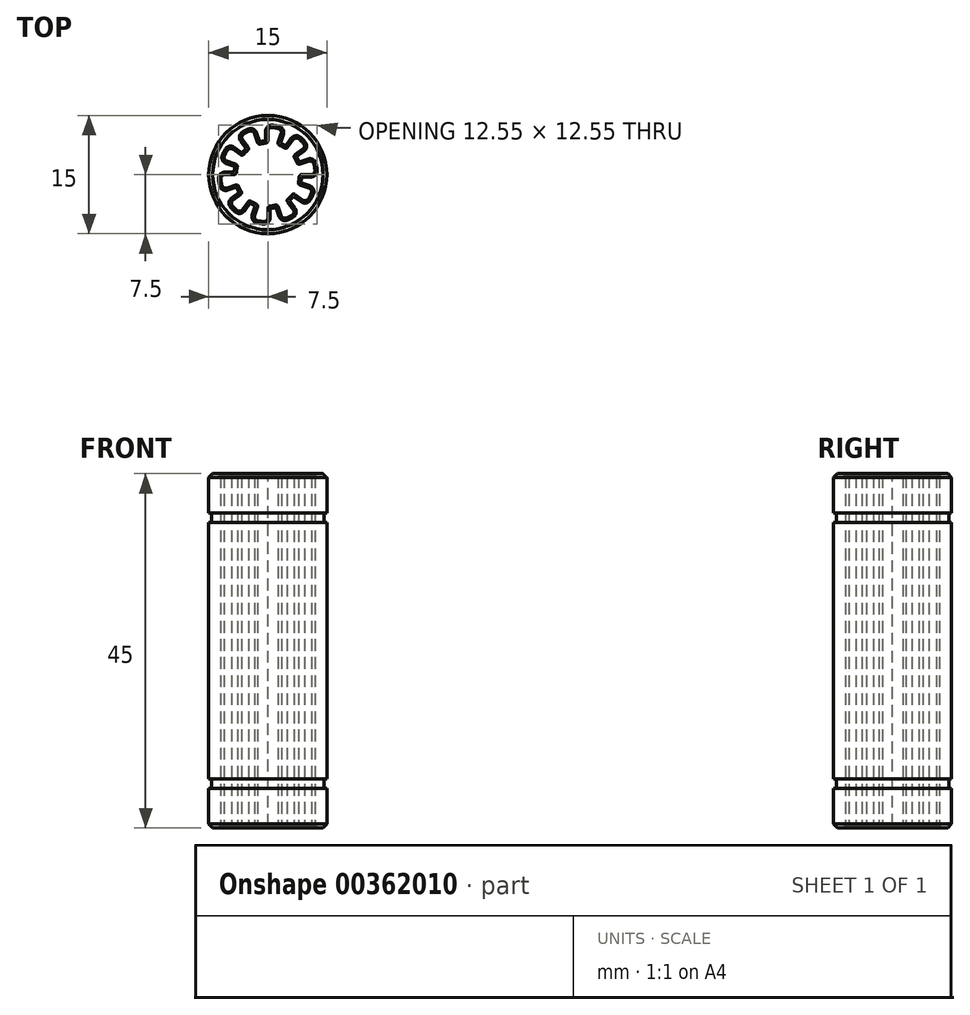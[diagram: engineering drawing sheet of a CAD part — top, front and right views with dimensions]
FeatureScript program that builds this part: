
annotation { "Feature Type Name" : "Feature", "Feature Type Description" : "" }
export const myFeature = defineFeature(function(context is Context, id is Id, definition is map)
    precondition{}
    {
        {
            var Q0;
            Q0=qCreatedBy(makeId("Top.planeOp"),FACE);
            var sketch = newSketch(context, id + "F0", { "sketchPlane" : qUnion([Q0])});
            skCircle(sketch, "E0", {"center": v(0, 0) * mm, "radius": 7.5 * mm});
            skLineSegment(sketch, "E1", {"start": v(0, 0) * mm, "end": v(0, 8.95) * mm, "construction": true});
            skLineSegment(sketch, "E2", {"start": v(0, 0) * mm, "end": v(5.23, 7.2) * mm, "construction": true});
            skArc(sketch, "E3", {"start": v(2.35, 3.24) * mm, "mid": v(1.82, 3.56) * mm, "end": v(1.24, 3.8) * mm});
            skArc(sketch, "E4", {"start": v(0, 6) * mm, "mid": v(0.94, 5.93) * mm, "end": v(1.85, 5.7) * mm});
            skLineSegment(sketch, "E5", {"start": v(1.85, 5.7) * mm, "end": v(1.24, 3.8) * mm});
            skLineSegment(sketch, "E6", {"start": v(2.35, 3.24) * mm, "end": v(3.53, 4.85) * mm});
            skArc(sketch, "E7", {"start": v(1.85, 5.7) * mm, "mid": v(2.72, 5.35) * mm, "end": v(3.53, 4.85) * mm, "construction": true});
            skLineSegment(sketch, "E8.1.0", {"start": v(0, 4) * mm, "end": v(0, 6) * mm});
            skArc(sketch, "E8.1.1", {"start": v(0, 4) * mm, "mid": v(-0.63, 3.95) * mm, "end": v(-1.24, 3.8) * mm});
            skLineSegment(sketch, "E8.1.2", {"start": v(-1.85, 5.7) * mm, "end": v(-1.24, 3.8) * mm});
            skArc(sketch, "E8.1.3", {"start": v(-3.53, 4.85) * mm, "mid": v(-2.72, 5.35) * mm, "end": v(-1.85, 5.7) * mm});
            skLineSegment(sketch, "E8.2.0", {"start": v(-2.35, 3.24) * mm, "end": v(-3.53, 4.85) * mm});
            skArc(sketch, "E8.2.1", {"start": v(-2.35, 3.24) * mm, "mid": v(-2.83, 2.83) * mm, "end": v(-3.24, 2.35) * mm});
            skLineSegment(sketch, "E8.2.2", {"start": v(-4.85, 3.53) * mm, "end": v(-3.24, 2.35) * mm});
            skArc(sketch, "E8.2.3", {"start": v(-5.7, 1.85) * mm, "mid": v(-5.35, 2.72) * mm, "end": v(-4.85, 3.53) * mm});
            skLineSegment(sketch, "E8.3.0", {"start": v(-3.8, 1.24) * mm, "end": v(-5.7, 1.85) * mm});
            skArc(sketch, "E8.3.1", {"start": v(-3.8, 1.24) * mm, "mid": v(-3.95, 0.63) * mm, "end": v(-4, 0) * mm});
            skLineSegment(sketch, "E8.3.2", {"start": v(-6, 0) * mm, "end": v(-4, 0) * mm});
            skArc(sketch, "E8.3.3", {"start": v(-5.7, -1.85) * mm, "mid": v(-5.93, -0.94) * mm, "end": v(-6, 0) * mm});
            skLineSegment(sketch, "E8.4.0", {"start": v(-3.8, -1.24) * mm, "end": v(-5.7, -1.85) * mm});
            skArc(sketch, "E8.4.1", {"start": v(-3.8, -1.24) * mm, "mid": v(-3.56, -1.82) * mm, "end": v(-3.24, -2.35) * mm});
            skLineSegment(sketch, "E8.4.2", {"start": v(-4.85, -3.53) * mm, "end": v(-3.24, -2.35) * mm});
            skArc(sketch, "E8.4.3", {"start": v(-3.53, -4.85) * mm, "mid": v(-4.24, -4.24) * mm, "end": v(-4.85, -3.53) * mm});
            skLineSegment(sketch, "E8.5.0", {"start": v(-2.35, -3.24) * mm, "end": v(-3.53, -4.85) * mm});
            skArc(sketch, "E8.5.1", {"start": v(-2.35, -3.24) * mm, "mid": v(-1.82, -3.56) * mm, "end": v(-1.24, -3.8) * mm});
            skLineSegment(sketch, "E8.5.2", {"start": v(-1.85, -5.7) * mm, "end": v(-1.24, -3.8) * mm});
            skArc(sketch, "E8.5.3", {"start": v(0, -6) * mm, "mid": v(-0.94, -5.93) * mm, "end": v(-1.85, -5.7) * mm});
            skLineSegment(sketch, "E8.6.0", {"start": v(0, -4) * mm, "end": v(0, -6) * mm});
            skArc(sketch, "E8.6.1", {"start": v(0, -4) * mm, "mid": v(0.63, -3.95) * mm, "end": v(1.24, -3.8) * mm});
            skLineSegment(sketch, "E8.6.2", {"start": v(1.85, -5.7) * mm, "end": v(1.24, -3.8) * mm});
            skArc(sketch, "E8.6.3", {"start": v(3.53, -4.85) * mm, "mid": v(2.72, -5.35) * mm, "end": v(1.85, -5.7) * mm});
            skLineSegment(sketch, "E8.7.0", {"start": v(2.35, -3.24) * mm, "end": v(3.53, -4.85) * mm});
            skArc(sketch, "E8.7.1", {"start": v(2.35, -3.24) * mm, "mid": v(2.83, -2.83) * mm, "end": v(3.24, -2.35) * mm});
            skLineSegment(sketch, "E8.7.2", {"start": v(4.85, -3.53) * mm, "end": v(3.24, -2.35) * mm});
            skArc(sketch, "E8.7.3", {"start": v(5.7, -1.85) * mm, "mid": v(5.35, -2.72) * mm, "end": v(4.85, -3.53) * mm});
            skLineSegment(sketch, "E8.8.0", {"start": v(3.8, -1.24) * mm, "end": v(5.7, -1.85) * mm});
            skArc(sketch, "E8.8.1", {"start": v(3.8, -1.24) * mm, "mid": v(3.95, -0.63) * mm, "end": v(4, 0) * mm});
            skLineSegment(sketch, "E8.8.2", {"start": v(6, 0) * mm, "end": v(4, 0) * mm});
            skArc(sketch, "E8.8.3", {"start": v(5.7, 1.85) * mm, "mid": v(5.93, 0.94) * mm, "end": v(6, 0) * mm});
            skLineSegment(sketch, "E8.9.0", {"start": v(3.8, 1.24) * mm, "end": v(5.7, 1.85) * mm});
            skArc(sketch, "E8.9.1", {"start": v(3.8, 1.24) * mm, "mid": v(3.56, 1.82) * mm, "end": v(3.24, 2.35) * mm});
            skLineSegment(sketch, "E8.9.2", {"start": v(4.85, 3.53) * mm, "end": v(3.24, 2.35) * mm});
            skArc(sketch, "E8.9.3", {"start": v(3.53, 4.85) * mm, "mid": v(4.24, 4.24) * mm, "end": v(4.85, 3.53) * mm});
            skSolve(sketch);
        }
        {
            var Q0;
            Q0=makeQuery(id+"F0.imprint","IMPRINT",FACE,{"disambiguationData":[TD([[makeQuery(id+"F0.imprint","IMPRINT",EDGE,{"derivedFrom":sQuery(id+"F0.wireOp",EDGE,"E0")}),1.0]])]});
            extrude(context, id + "F1", {"entities" : qUnion([Q0]), "depth" : 45 * mm});
        }
        {
            var Q0;
            Q0=qCreatedBy(makeId("Top.planeOp"),FACE);
            cPlane(context, id + "F2", {"entities" : qUnion([Q0]), "cplaneType" : CPlaneType.OFFSET, "offset" : 5 * mm, "width" : 150 * mm, "height" : 150 * mm});
        }
        {
            var Q0;
            Q0=qCreatedBy(id+"F2.planeOp",FACE);
            var sketch = newSketch(context, id + "F3", { "sketchPlane" : qUnion([Q0])});
            skCircle(sketch, "E9", {"center": v(0, 0) * mm, "radius": 7.15 * mm});
            skCircle(sketch, "E10", {"center": v(0, 0) * mm, "radius": 8 * mm});
            skSolve(sketch);
        }
        {
            var Q0;
            Q0 = qSketchRegion(id + "F3", true);
            extrude(context, id + "F4", {"entities" : qUnion([Q0]), "operationType" : NewBodyOperationType.REMOVE, "depth" : 1.2 * mm});
        }
        {
            var Q0;
            Q0=qCreatedBy(makeId("Top.planeOp"),FACE);
            cPlane(context, id + "F5", {"entities" : qUnion([Q0]), "cplaneType" : CPlaneType.OFFSET, "offset" : (45 - 5) * mm, "width" : 150 * mm, "height" : 150 * mm});
        }
        {
            var Q0;
            Q0=qCreatedBy(id+"F5.planeOp",FACE);
            var sketch = newSketch(context, id + "F6", { "sketchPlane" : qUnion([Q0])});
            skCircle(sketch, "E11", {"center": v(0, 0) * mm, "radius": 8 * mm});
            skCircle(sketch, "E12", {"center": v(0, 0) * mm, "radius": 7.15 * mm});
            skSolve(sketch);
        }
        {
            var Q0;
            Q0 = qSketchRegion(id + "F6", true);
            extrude(context, id + "F7", {"entities" : qUnion([Q0]), "operationType" : NewBodyOperationType.REMOVE, "oppositeDirection" : true, "depth" : 1.2 * mm});
        }
        {
            var Q0;
            Q0=makeQuery(id+"F1.opExtrude","CAP_EDGE",EDGE,{"disambiguationData":[OSD([sQuery(id+"F0.wireOp",EDGE,"E0")])],"isStart":false});
            var Q1;
            Q1=makeQuery(id+"F1.opExtrude","CAP_EDGE",EDGE,{"disambiguationData":[OSD([sQuery(id+"F0.wireOp",EDGE,"E0")])],"isStart":true});
            chamfer(context, id + "F8", {"entities" : qUnion([Q0, Q1]), "width" : 0.5 * mm, "tangentPropagation" : true});
        }
        {
            var Q0;
            Q0=makeQuery(id+"F1.opExtrude","SWEPT_EDGE",EDGE,{"disambiguationData":[OSD([sQuery(id+"F0.wireOp",EDGE,"E3"),sQuery(id+"F0.wireOp",EDGE,"E6")])]});
            var Q1;
            Q1=makeQuery(id+"F1.opExtrude","SWEPT_EDGE",EDGE,{"disambiguationData":[OSD([sQuery(id+"F0.wireOp",EDGE,"E3"),sQuery(id+"F0.wireOp",EDGE,"E5")])]});
            var Q2;
            Q2=makeQuery(id+"F1.opExtrude","SWEPT_EDGE",EDGE,{"disambiguationData":[OSD([sQuery(id+"F0.wireOp",EDGE,"045b818b-034f-4962-901c-0fb9900f9058.3.11.0"),sQuery(id+"F0.wireOp",EDGE,"045b818b-034f-4962-901c-0fb9900f9058.7.11.0")])]});
            var Q3;
            Q3=makeQuery(id+"F1.opExtrude","SWEPT_EDGE",EDGE,{"disambiguationData":[OSD([sQuery(id+"F0.wireOp",EDGE,"045b818b-034f-4962-901c-0fb9900f9058.3.11.0"),sQuery(id+"F0.wireOp",EDGE,"045b818b-034f-4962-901c-0fb9900f9058.6.11.0")])]});
            var Q4;
            Q4=makeQuery(id+"F1.opExtrude","SWEPT_EDGE",EDGE,{"disambiguationData":[OSD([sQuery(id+"F0.wireOp",EDGE,"045b818b-034f-4962-901c-0fb9900f9058.3.10.0"),sQuery(id+"F0.wireOp",EDGE,"045b818b-034f-4962-901c-0fb9900f9058.7.10.0")])]});
            var Q5;
            Q5=makeQuery(id+"F1.opExtrude","SWEPT_EDGE",EDGE,{"disambiguationData":[OSD([sQuery(id+"F0.wireOp",EDGE,"045b818b-034f-4962-901c-0fb9900f9058.3.10.0"),sQuery(id+"F0.wireOp",EDGE,"045b818b-034f-4962-901c-0fb9900f9058.6.10.0")])]});
            var Q6;
            Q6=makeQuery(id+"F1.opExtrude","SWEPT_EDGE",EDGE,{"disambiguationData":[OSD([sQuery(id+"F0.wireOp",EDGE,"E8.9.1"),sQuery(id+"F0.wireOp",EDGE,"E8.9.2")])]});
            var Q7;
            Q7=makeQuery(id+"F1.opExtrude","SWEPT_EDGE",EDGE,{"disambiguationData":[OSD([sQuery(id+"F0.wireOp",EDGE,"E8.9.0"),sQuery(id+"F0.wireOp",EDGE,"E8.9.1")])]});
            var Q8;
            Q8=makeQuery(id+"F1.opExtrude","SWEPT_EDGE",EDGE,{"disambiguationData":[OSD([sQuery(id+"F0.wireOp",EDGE,"E8.8.1"),sQuery(id+"F0.wireOp",EDGE,"E8.8.2")])]});
            var Q9;
            Q9=makeQuery(id+"F1.opExtrude","SWEPT_EDGE",EDGE,{"disambiguationData":[OSD([sQuery(id+"F0.wireOp",EDGE,"E8.8.0"),sQuery(id+"F0.wireOp",EDGE,"E8.8.1")])]});
            var Q10;
            Q10=makeQuery(id+"F1.opExtrude","SWEPT_EDGE",EDGE,{"disambiguationData":[OSD([sQuery(id+"F0.wireOp",EDGE,"E8.7.1"),sQuery(id+"F0.wireOp",EDGE,"E8.7.2")])]});
            var Q11;
            Q11=makeQuery(id+"F1.opExtrude","SWEPT_EDGE",EDGE,{"disambiguationData":[OSD([sQuery(id+"F0.wireOp",EDGE,"E8.7.0"),sQuery(id+"F0.wireOp",EDGE,"E8.7.1")])]});
            var Q12;
            Q12=makeQuery(id+"F1.opExtrude","SWEPT_EDGE",EDGE,{"disambiguationData":[OSD([sQuery(id+"F0.wireOp",EDGE,"E8.6.1"),sQuery(id+"F0.wireOp",EDGE,"E8.6.2")])]});
            var Q13;
            Q13=makeQuery(id+"F1.opExtrude","SWEPT_EDGE",EDGE,{"disambiguationData":[OSD([sQuery(id+"F0.wireOp",EDGE,"E8.6.0"),sQuery(id+"F0.wireOp",EDGE,"E8.6.1")])]});
            var Q14;
            Q14=makeQuery(id+"F1.opExtrude","SWEPT_EDGE",EDGE,{"disambiguationData":[OSD([sQuery(id+"F0.wireOp",EDGE,"E8.5.1"),sQuery(id+"F0.wireOp",EDGE,"E8.5.2")])]});
            var Q15;
            Q15=makeQuery(id+"F1.opExtrude","SWEPT_EDGE",EDGE,{"disambiguationData":[OSD([sQuery(id+"F0.wireOp",EDGE,"E8.5.0"),sQuery(id+"F0.wireOp",EDGE,"E8.5.1")])]});
            var Q16;
            Q16=makeQuery(id+"F1.opExtrude","SWEPT_EDGE",EDGE,{"disambiguationData":[OSD([sQuery(id+"F0.wireOp",EDGE,"E8.4.1"),sQuery(id+"F0.wireOp",EDGE,"E8.4.2")])]});
            var Q17;
            Q17=makeQuery(id+"F1.opExtrude","SWEPT_EDGE",EDGE,{"disambiguationData":[OSD([sQuery(id+"F0.wireOp",EDGE,"E8.4.0"),sQuery(id+"F0.wireOp",EDGE,"E8.4.1")])]});
            var Q18;
            Q18=makeQuery(id+"F1.opExtrude","SWEPT_EDGE",EDGE,{"disambiguationData":[OSD([sQuery(id+"F0.wireOp",EDGE,"E8.3.1"),sQuery(id+"F0.wireOp",EDGE,"E8.3.2")])]});
            var Q19;
            Q19=makeQuery(id+"F1.opExtrude","SWEPT_EDGE",EDGE,{"disambiguationData":[OSD([sQuery(id+"F0.wireOp",EDGE,"E8.3.0"),sQuery(id+"F0.wireOp",EDGE,"E8.3.1")])]});
            var Q20;
            Q20=makeQuery(id+"F1.opExtrude","SWEPT_EDGE",EDGE,{"disambiguationData":[OSD([sQuery(id+"F0.wireOp",EDGE,"E8.2.1"),sQuery(id+"F0.wireOp",EDGE,"E8.2.2")])]});
            var Q21;
            Q21=makeQuery(id+"F1.opExtrude","SWEPT_EDGE",EDGE,{"disambiguationData":[OSD([sQuery(id+"F0.wireOp",EDGE,"E8.2.0"),sQuery(id+"F0.wireOp",EDGE,"E8.2.1")])]});
            var Q22;
            Q22=makeQuery(id+"F1.opExtrude","SWEPT_EDGE",EDGE,{"disambiguationData":[OSD([sQuery(id+"F0.wireOp",EDGE,"E8.1.1"),sQuery(id+"F0.wireOp",EDGE,"E8.1.2")])]});
            var Q23;
            Q23=makeQuery(id+"F1.opExtrude","SWEPT_EDGE",EDGE,{"disambiguationData":[OSD([sQuery(id+"F0.wireOp",EDGE,"E8.1.0"),sQuery(id+"F0.wireOp",EDGE,"E8.1.1")])]});
            fillet(context, id + "F9", {"entities" : qUnion([Q0, Q1, Q2, Q3, Q4, Q5, Q6, Q7, Q8, Q9, Q10, Q11, Q12, Q13, Q14, Q15, Q16, Q17, Q18, Q19, Q20, Q21, Q22, Q23]), "radius" : 0.3 * mm, "tangentPropagation" : true, "allowEdgeOverflow" : false});
        }
        {
            var Q0;
            Q0=makeQuery(id+"F1.opExtrude","SWEPT_EDGE",EDGE,{"disambiguationData":[OSD([sQuery(id+"F0.wireOp",EDGE,"045b818b-034f-4962-901c-0fb9900f9058.7.11.0"),sQuery(id+"F0.wireOp",EDGE,"045b818b-034f-4962-901c-0fb9900f9058.10.11.0")])]});
            var Q1;
            Q1=makeQuery(id+"F1.opExtrude","SWEPT_EDGE",EDGE,{"disambiguationData":[OSD([sQuery(id+"F0.wireOp",EDGE,"E6"),sQuery(id+"F0.wireOp",EDGE,"045b818b-034f-4962-901c-0fb9900f9058.10.11.0")])]});
            var Q2;
            Q2=makeQuery(id+"F1.opExtrude","SWEPT_EDGE",EDGE,{"disambiguationData":[OSD([sQuery(id+"F0.wireOp",EDGE,"E4"),sQuery(id+"F0.wireOp",EDGE,"E8.1.0")])]});
            var Q3;
            Q3=makeQuery(id+"F1.opExtrude","SWEPT_EDGE",EDGE,{"disambiguationData":[OSD([sQuery(id+"F0.wireOp",EDGE,"E4"),sQuery(id+"F0.wireOp",EDGE,"E5")])]});
            var Q4;
            Q4=makeQuery(id+"F1.opExtrude","SWEPT_EDGE",EDGE,{"disambiguationData":[OSD([sQuery(id+"F0.wireOp",EDGE,"045b818b-034f-4962-901c-0fb9900f9058.10.10.0"),sQuery(id+"F0.wireOp",EDGE,"045b818b-034f-4962-901c-0fb9900f9058.6.11.0")])]});
            var Q5;
            Q5=makeQuery(id+"F1.opExtrude","SWEPT_EDGE",EDGE,{"disambiguationData":[OSD([sQuery(id+"F0.wireOp",EDGE,"045b818b-034f-4962-901c-0fb9900f9058.7.10.0"),sQuery(id+"F0.wireOp",EDGE,"045b818b-034f-4962-901c-0fb9900f9058.10.10.0")])]});
            var Q6;
            Q6=makeQuery(id+"F1.opExtrude","SWEPT_EDGE",EDGE,{"disambiguationData":[OSD([sQuery(id+"F0.wireOp",EDGE,"E8.9.3"),sQuery(id+"F0.wireOp",EDGE,"045b818b-034f-4962-901c-0fb9900f9058.6.10.0")])]});
            var Q7;
            Q7=makeQuery(id+"F1.opExtrude","SWEPT_EDGE",EDGE,{"disambiguationData":[OSD([sQuery(id+"F0.wireOp",EDGE,"E8.9.2"),sQuery(id+"F0.wireOp",EDGE,"E8.9.3")])]});
            var Q8;
            Q8=makeQuery(id+"F1.opExtrude","SWEPT_EDGE",EDGE,{"disambiguationData":[OSD([sQuery(id+"F0.wireOp",EDGE,"E8.8.3"),sQuery(id+"F0.wireOp",EDGE,"E8.9.0")])]});
            var Q9;
            Q9=makeQuery(id+"F1.opExtrude","SWEPT_EDGE",EDGE,{"disambiguationData":[OSD([sQuery(id+"F0.wireOp",EDGE,"E8.8.2"),sQuery(id+"F0.wireOp",EDGE,"E8.8.3")])]});
            var Q10;
            Q10=makeQuery(id+"F1.opExtrude","SWEPT_EDGE",EDGE,{"disambiguationData":[OSD([sQuery(id+"F0.wireOp",EDGE,"E8.7.3"),sQuery(id+"F0.wireOp",EDGE,"E8.8.0")])]});
            var Q11;
            Q11=makeQuery(id+"F1.opExtrude","SWEPT_EDGE",EDGE,{"disambiguationData":[OSD([sQuery(id+"F0.wireOp",EDGE,"E8.7.2"),sQuery(id+"F0.wireOp",EDGE,"E8.7.3")])]});
            var Q12;
            Q12=makeQuery(id+"F1.opExtrude","SWEPT_EDGE",EDGE,{"disambiguationData":[OSD([sQuery(id+"F0.wireOp",EDGE,"E8.6.3"),sQuery(id+"F0.wireOp",EDGE,"E8.7.0")])]});
            var Q13;
            Q13=makeQuery(id+"F1.opExtrude","SWEPT_EDGE",EDGE,{"disambiguationData":[OSD([sQuery(id+"F0.wireOp",EDGE,"E8.6.2"),sQuery(id+"F0.wireOp",EDGE,"E8.6.3")])]});
            var Q14;
            Q14=makeQuery(id+"F1.opExtrude","SWEPT_EDGE",EDGE,{"disambiguationData":[OSD([sQuery(id+"F0.wireOp",EDGE,"E8.5.2"),sQuery(id+"F0.wireOp",EDGE,"E8.5.3")])]});
            var Q15;
            Q15=makeQuery(id+"F1.opExtrude","SWEPT_EDGE",EDGE,{"disambiguationData":[OSD([sQuery(id+"F0.wireOp",EDGE,"E8.5.3"),sQuery(id+"F0.wireOp",EDGE,"E8.6.0")])]});
            var Q16;
            Q16=makeQuery(id+"F1.opExtrude","SWEPT_EDGE",EDGE,{"disambiguationData":[OSD([sQuery(id+"F0.wireOp",EDGE,"E8.4.3"),sQuery(id+"F0.wireOp",EDGE,"E8.5.0")])]});
            var Q17;
            Q17=makeQuery(id+"F1.opExtrude","SWEPT_EDGE",EDGE,{"disambiguationData":[OSD([sQuery(id+"F0.wireOp",EDGE,"E8.4.2"),sQuery(id+"F0.wireOp",EDGE,"E8.4.3")])]});
            var Q18;
            Q18=makeQuery(id+"F1.opExtrude","SWEPT_EDGE",EDGE,{"disambiguationData":[OSD([sQuery(id+"F0.wireOp",EDGE,"E8.3.3"),sQuery(id+"F0.wireOp",EDGE,"E8.4.0")])]});
            var Q19;
            Q19=makeQuery(id+"F1.opExtrude","SWEPT_EDGE",EDGE,{"disambiguationData":[OSD([sQuery(id+"F0.wireOp",EDGE,"E8.3.2"),sQuery(id+"F0.wireOp",EDGE,"E8.3.3")])]});
            var Q20;
            Q20=makeQuery(id+"F1.opExtrude","SWEPT_EDGE",EDGE,{"disambiguationData":[OSD([sQuery(id+"F0.wireOp",EDGE,"E8.2.3"),sQuery(id+"F0.wireOp",EDGE,"E8.3.0")])]});
            var Q21;
            Q21=makeQuery(id+"F1.opExtrude","SWEPT_EDGE",EDGE,{"disambiguationData":[OSD([sQuery(id+"F0.wireOp",EDGE,"E8.2.2"),sQuery(id+"F0.wireOp",EDGE,"E8.2.3")])]});
            var Q22;
            Q22=makeQuery(id+"F1.opExtrude","SWEPT_EDGE",EDGE,{"disambiguationData":[OSD([sQuery(id+"F0.wireOp",EDGE,"E8.1.3"),sQuery(id+"F0.wireOp",EDGE,"E8.2.0")])]});
            var Q23;
            Q23=makeQuery(id+"F1.opExtrude","SWEPT_EDGE",EDGE,{"disambiguationData":[OSD([sQuery(id+"F0.wireOp",EDGE,"E8.1.2"),sQuery(id+"F0.wireOp",EDGE,"E8.1.3")])]});
            fillet(context, id + "F10", {"entities" : qUnion([Q0, Q1, Q2, Q3, Q4, Q5, Q6, Q7, Q8, Q9, Q10, Q11, Q12, Q13, Q14, Q15, Q16, Q17, Q18, Q19, Q20, Q21, Q22, Q23]), "radius" : 0.5 * mm, "tangentPropagation" : true, "allowEdgeOverflow" : false});
        }
        {
            var Q0;
            Q0=makeQuery(id+"F1.opExtrude","CAP_EDGE",EDGE,{"disambiguationData":[OSD([sQuery(id+"F0.wireOp",EDGE,"E8.2.2")])],"isStart":false});
            var Q1;
            Q1=makeQuery(id+"F1.opExtrude","CAP_EDGE",EDGE,{"disambiguationData":[OSD([sQuery(id+"F0.wireOp",EDGE,"E5")])],"isStart":true});
            chamfer(context, id + "F11", {"entities" : qUnion([Q0, Q1]), "width" : 0.3 * mm, "tangentPropagation" : true});
        }
    });
